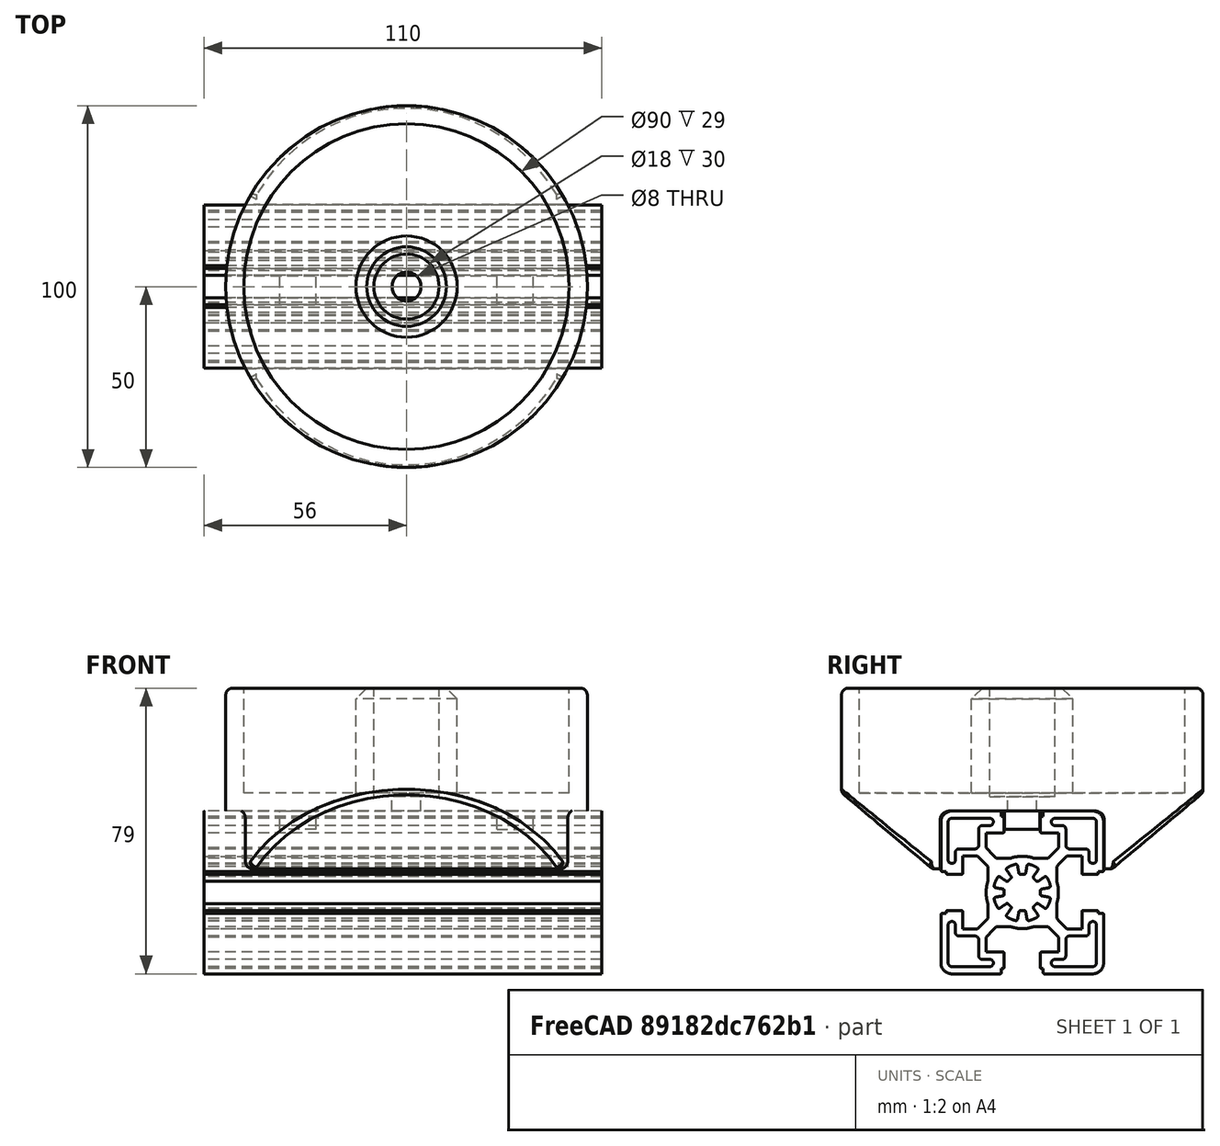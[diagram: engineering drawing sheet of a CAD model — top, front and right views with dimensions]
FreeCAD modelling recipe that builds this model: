
FCSTD DOCUMENT  (FreeCAD 0.18R4 (GitTag))
Label: damper
License: All rights reserved
LicenseURL: http://en.wikipedia.org/wiki/All_rights_reserved
objects: Part::Cylinder×5, Part::MultiFuse×5, Part::Cut×4, Part::Box×3, Part::Mirroring×2, Part::Fillet×2, Part::FeaturePython×1, Part::Chamfer×1
note: 23 computed .brp shape members not serialized (recipe doc carries the construction recipe); baked Part::Feature solids carry a one-line shape summary decoded from their .brp

FEATURE [Part::Cylinder] Cylinder  label="Cilindro"
  Angle = 360
  AttacherType = Attacher::AttachEngine3D
  Height = 35
  Placement = pos=(0,0,5) rot=(0,0,1;0rad)
  Radius = 45
FEATURE [Part::Cylinder] Cylinder001  label="Cilindro001"
  Angle = 360
  AttacherType = Attacher::AttachEngine3D
  Height = 34
  Radius = 14
FEATURE [Part::Cylinder] Cylinder002  label="Cilindro002"
  Angle = 360
  AttacherType = Attacher::AttachEngine3D
  Height = 50
  Placement = pos=(0,0,-16) rot=(0,0,1;0rad)
  Radius = 50
FEATURE [Part::Cut] Cut
  Base = -> Cylinder002
  Refine = true
  Tool = -> Cylinder
FEATURE [Part::MultiFuse] Fusion
  Refine = true
  Shapes = -> [Cut,Cylinder001]
FEATURE [Part::FeaturePython] Clone015  label="Motedis_45x45_refined003"  # WARN: FeaturePython — macro-defined, semantics opaque (R4)
  AttacherType = Attacher::AttachEngine3D
  Fuse = false
  Placement = pos=(54,-22.5,-45) rot=(0,-1,0;1.5708rad)
  Scale = (1,1,0.11)
FEATURE [Part::Box] Box  label="Cubo"
  AttacherType = Attacher::AttachEngine3D
  Height = 21
  Length = 90
  Placement = pos=(-45,17,-50) rot=(1,0,0;0.698132rad)
  Width = 70
FEATURE [Part::Mirroring] Part__Mirroring  label="Cubo (Mirror #1)"
  Base = (0,0,0)
  Normal = (0,1,0)
  Source = -> Box
FEATURE [Part::MultiFuse] Fusion001
  Refine = true
  Shapes = -> [Box,Part__Mirroring]
FEATURE [Part::Cut] Cut001
  Base = -> Fusion
  Refine = true
  Tool = -> Fusion001
FEATURE [Part::Box] Box001  label="Cubo001"
  AttacherType = Attacher::AttachEngine3D
  Height = 20
  Length = 100
  Placement = pos=(-50,-22.7,-20) rot=(0,0,1;0rad)
  Width = 45.4
FEATURE [Part::Cut] Cut002
  Base = -> Cut001
  Refine = true
  Tool = -> Box001
FEATURE [Part::Cylinder] Cylinder003  label="Cilindro003"
  Angle = 360
  AttacherType = Attacher::AttachEngine3D
  Height = 10
  Placement = pos=(0,0,-2) rot=(0,0,1;0rad)
  Radius = 4
FEATURE [Part::Cylinder] Cylinder004  label="Cilindro004"
  Angle = 360
  AttacherType = Attacher::AttachEngine3D
  Height = 35
  Placement = pos=(0,0,4) rot=(0,0,1;0rad)
  Radius = 9
FEATURE [Part::MultiFuse] Fusion002
  Refine = true
  Shapes = -> [Cylinder003,Cylinder004]
FEATURE [Part::Cut] Cut003
  Base = -> Cut002
  Refine = true
  Tool = -> Fusion002
FEATURE [Part::Fillet] Fillet
  Base = -> Cut003
  Edges = 2 edges r=2.5: [Edge29,Edge30]
FEATURE [Part::Box] Box002  label="Cubo002"
  AttacherType = Attacher::AttachEngine3D
  Height = 10
  Length = 10
  Placement = pos=(25,-4.9,-5) rot=(0,0,1;0rad)
  Width = 9.8
FEATURE [Part::Mirroring] Part__Mirroring001  label="Cubo002 (Mirror #2)"
  Base = (0,0,0)
  Normal = (1,0,0)
  Source = -> Box002
FEATURE [Part::MultiFuse] Fusion003
  Refine = true
  Shapes = -> [Box002,Part__Mirroring001]
FEATURE [Part::MultiFuse] Fusion004
  Refine = true
  Shapes = -> [Fillet,Fusion003]
FEATURE [Part::Fillet] Fillet001
  Base = -> Fusion004
  Edges = 9 edges r=2: [Edge9,Edge10,Edge11,Edge13,Edge18,Edge20,Edge22,Edge39,Edge42]
FEATURE [Part::Chamfer] Chamfer
  Base = -> Fillet001
  Edges = 1 edges r=3: [Edge94]
